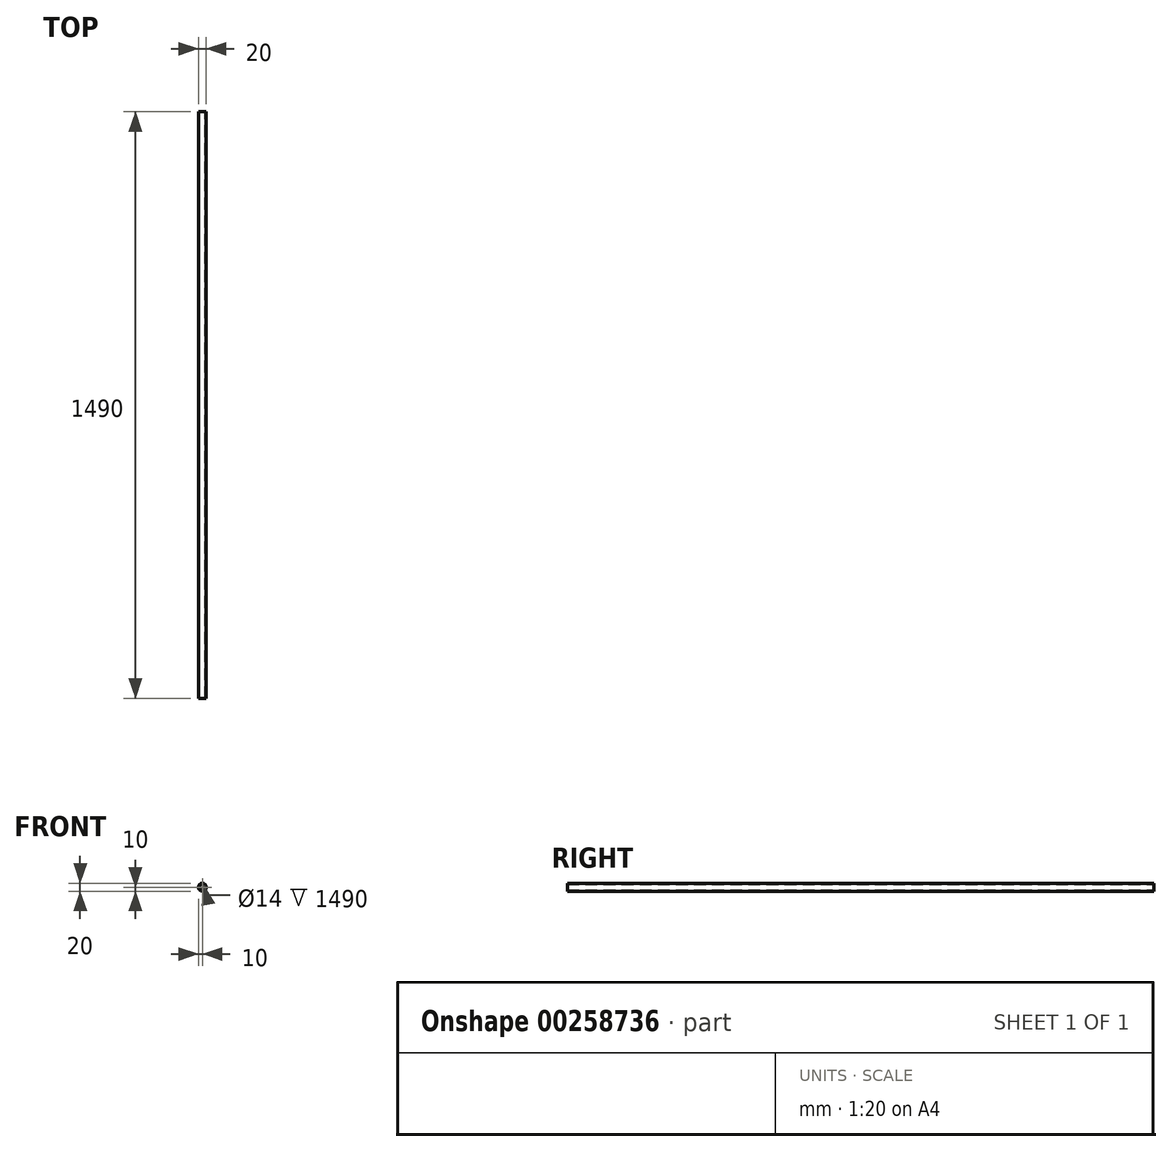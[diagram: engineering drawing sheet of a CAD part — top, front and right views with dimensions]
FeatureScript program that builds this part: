
annotation { "Feature Type Name" : "Feature", "Feature Type Description" : "" }
export const myFeature = defineFeature(function(context is Context, id is Id, definition is map)
    precondition{}
    {
        {
            var Q0;
            Q0=qCreatedBy(makeId("Front.planeOp"),FACE);
            var sketch = newSketch(context, id + "F0", { "sketchPlane" : qUnion([Q0])});
            skCircle(sketch, "E0", {"center": v(0, 0) * mm, "radius": 10 * mm});
            skCircle(sketch, "E1", {"center": v(0, 0) * mm, "radius": 7 * mm});
            skSolve(sketch);
        }
        {
            var Q0;
            Q0=makeQuery(id+"F0.imprint","IMPRINT",FACE,{"disambiguationData":[TD([[makeQuery(id+"F0.imprint","IMPRINT",EDGE,{"derivedFrom":sQuery(id+"F0.wireOp",EDGE,"E0")}),1.0]])]});
            extrude(context, id + "F1", {"entities" : qUnion([Q0]), "depth" : 1490 * mm});
        }
    });
